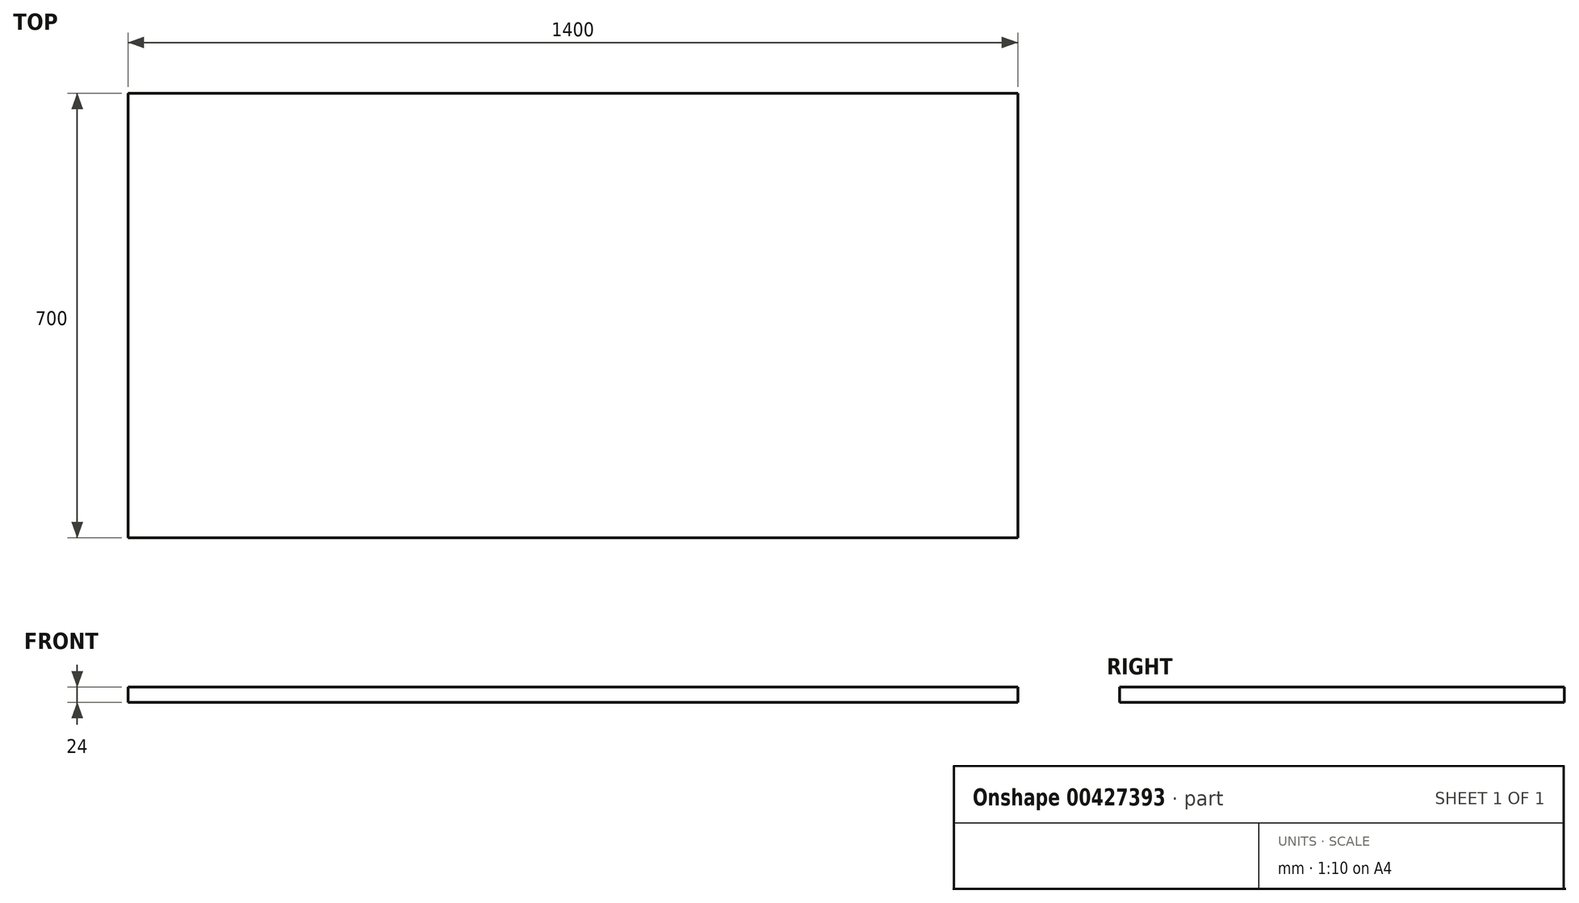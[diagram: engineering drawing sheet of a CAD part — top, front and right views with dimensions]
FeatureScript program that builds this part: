
annotation { "Feature Type Name" : "Feature", "Feature Type Description" : "" }
export const myFeature = defineFeature(function(context is Context, id is Id, definition is map)
    precondition{}
    {
        {
            var Q0;
            Q0=qCreatedBy(makeId("Top.planeOp"),FACE);
            var sketch = newSketch(context, id + "F0", { "sketchPlane" : qUnion([Q0])});
            skLineSegment(sketch, "E0.bottom", {"start": v(700, 350) * mm, "end": v(-700, 350) * mm});
            skLineSegment(sketch, "E0.top", {"start": v(700, -350) * mm, "end": v(-700, -350) * mm});
            skLineSegment(sketch, "E0.left", {"start": v(700, 350) * mm, "end": v(700, -350) * mm});
            skLineSegment(sketch, "E0.right", {"start": v(-700, 350) * mm, "end": v(-700, -350) * mm});
            skPoint(sketch, "E0.middle", {"position": v(0, 0) * mm});
            skSolve(sketch);
        }
        {
            var Q0;
            Q0=makeQuery(id+"F0.imprint","IMPRINT",FACE,{"disambiguationData":[TD([[makeQuery(id+"F0.imprint","IMPRINT",EDGE,{"derivedFrom":sQuery(id+"F0.wireOp",EDGE,"E0.bottom")}),1.0]])]});
            extrude(context, id + "F1", {"entities" : qUnion([Q0]), "depth" : 24 * mm});
        }
    });
